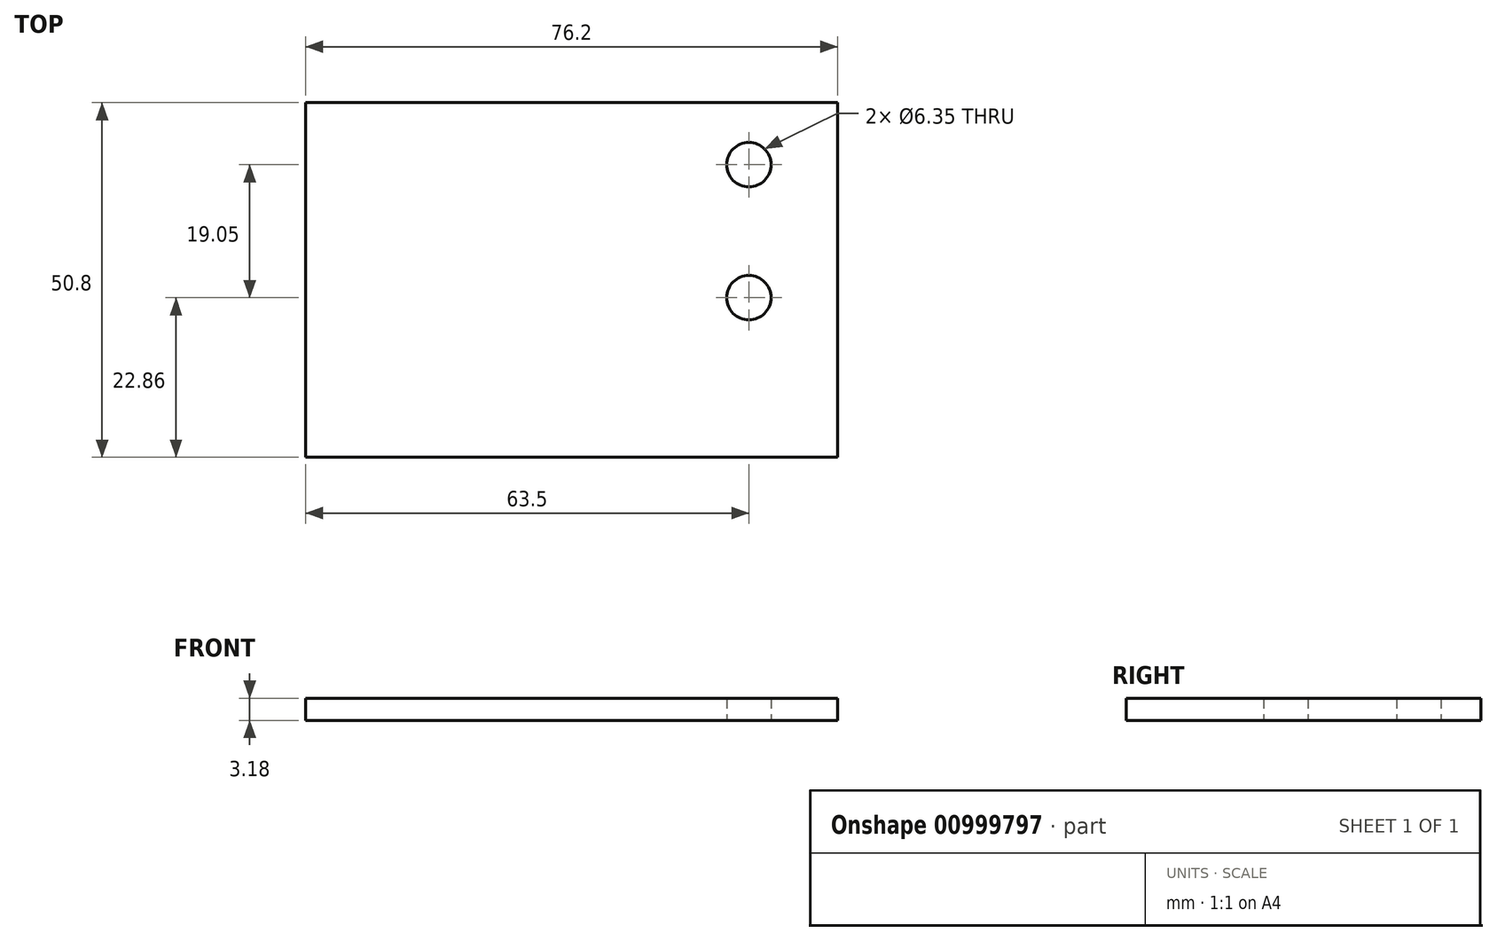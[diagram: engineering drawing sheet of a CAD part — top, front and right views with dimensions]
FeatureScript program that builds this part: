
annotation { "Feature Type Name" : "Feature", "Feature Type Description" : "" }
export const myFeature = defineFeature(function(context is Context, id is Id, definition is map)
    precondition{}
    {
        {
            var Q0;
            Q0=qCreatedBy(makeId("Top.planeOp"),FACE);
            var sketch = newSketch(context, id + "F0", { "sketchPlane" : qUnion([Q0])});
            skLineSegment(sketch, "E0.bottom", {"start": v(38.1, 25.4) * mm, "end": v(-38.1, 25.4) * mm});
            skLineSegment(sketch, "E0.top", {"start": v(38.1, -25.4) * mm, "end": v(-38.1, -25.4) * mm});
            skLineSegment(sketch, "E0.left", {"start": v(38.1, 25.4) * mm, "end": v(38.1, -25.4) * mm});
            skLineSegment(sketch, "E0.right", {"start": v(-38.1, 25.4) * mm, "end": v(-38.1, -25.4) * mm});
            skPoint(sketch, "E0.middle", {"position": v(0, 0) * mm});
            skCircle(sketch, "E1", {"center": v(25.4, 16.51) * mm, "radius": 3.18 * mm});
            skCircle(sketch, "E2", {"center": v(25.4, -2.54) * mm, "radius": 3.18 * mm});
            skSolve(sketch);
        }
        {
            var Q0;
            Q0=makeQuery(id+"F0.imprint","IMPRINT",FACE,{"disambiguationData":[TD([[makeQuery(id+"F0.imprint","IMPRINT",EDGE,{"derivedFrom":sQuery(id+"F0.wireOp",EDGE,"E0.bottom")}),1.0]])]});
            extrude(context, id + "F1", {"entities" : qUnion([Q0]), "depth" : 3.17 * mm, "offsetDistance" : 25.4 * mm, "symmetric" : true});
        }
    });
